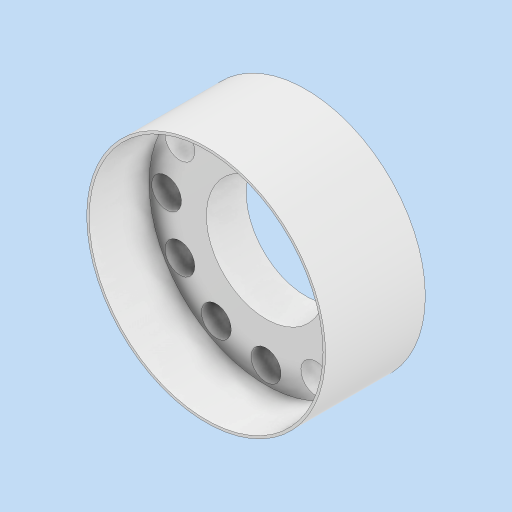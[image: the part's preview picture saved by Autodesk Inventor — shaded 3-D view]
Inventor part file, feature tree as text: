
AUTODESK INVENTOR PART (.ipt)
format: ipt  version: 2023 (Build 270158000, 158)  size: 176,640 bytes
history: native  units: in
note: dims shown in document units (in); Inventor stores cm internally (conversion verified against a paired STEP export)
features: extrude x3, sketch x1, pattern_circular x1
ambient origin geometry x8: Origin, YZ Plane, XZ Plane, XY Plane, X Axis, Y Axis, Z Axis, Center Point
bodies: Solid1 (feature_tree)
feature tree (5):
  sketch  "Sketch1"  dims[d0=3.0in d1=0.0315in d2=1.253in d3=0.0in d4=1.5in d5=0.5in d6=0.0in d7=2.5in d8=0.375in d9=0.5in d10=0.0in d11=4.7244in d12=360.0deg]
  extrude  "Extrusion1"  Depth=0.5in
  extrude  "Extrusion2"  Depth=1.253in TaperAngle=0.0deg
  extrude  "Extrusion3"  Depth=1.5in
  pattern_circular  "Circular Pattern1"  [2 undecoded]
note: 2 required parameter values undecoded (feature->parameter linkage not recoverable at this tier; creation-order binding heuristic only, values carry confidence <= 0.55)
